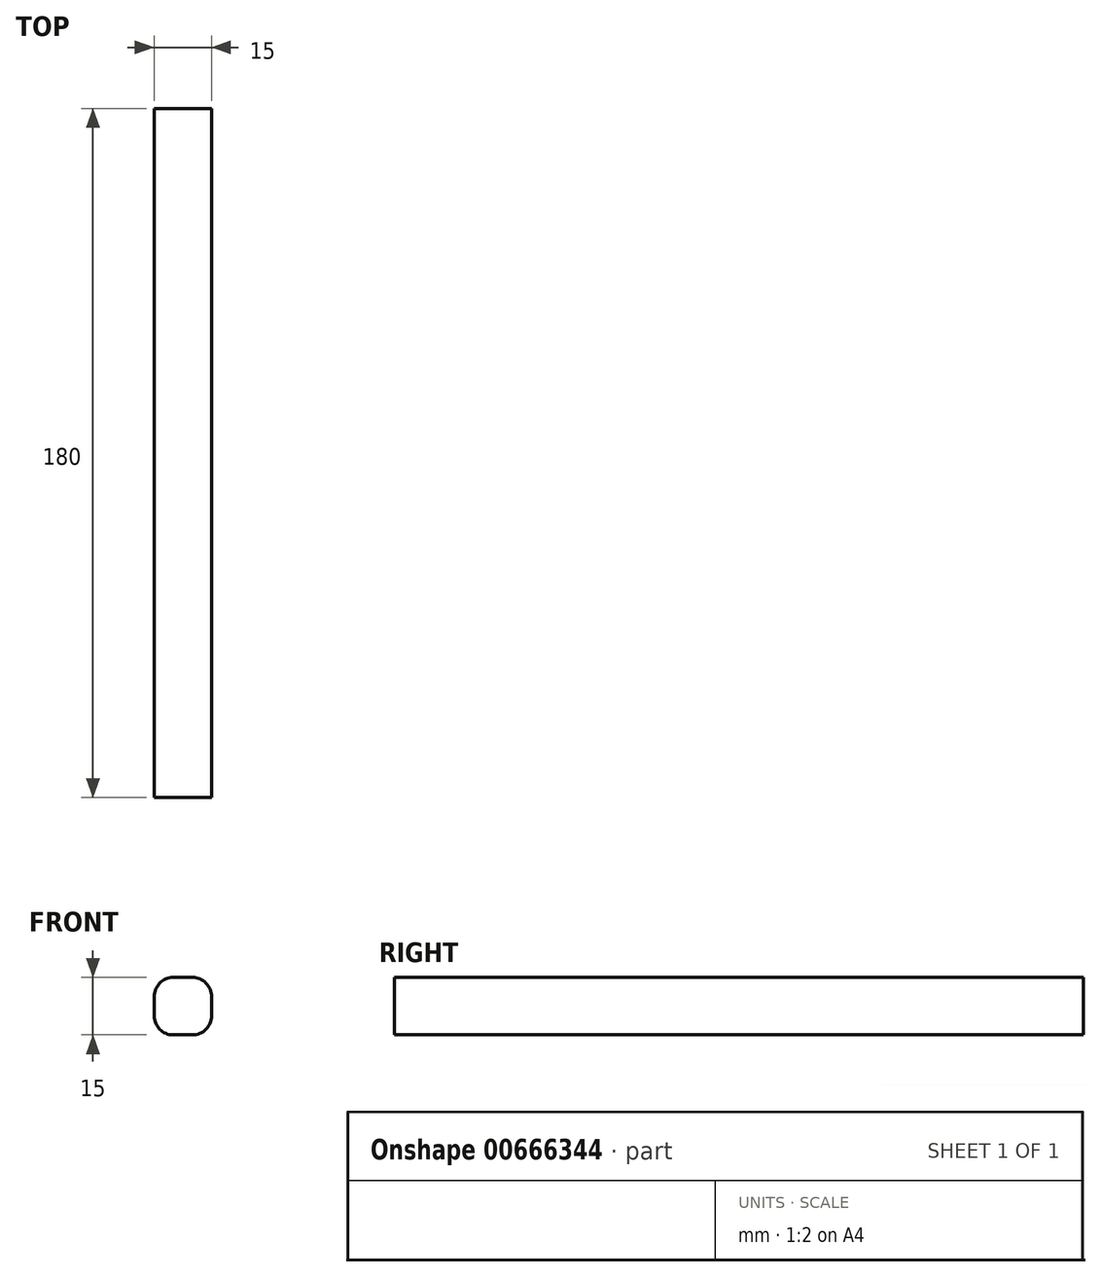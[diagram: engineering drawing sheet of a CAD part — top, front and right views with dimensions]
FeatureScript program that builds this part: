
annotation { "Feature Type Name" : "Feature", "Feature Type Description" : "" }
export const myFeature = defineFeature(function(context is Context, id is Id, definition is map)
    precondition{}
    {
        {
            var Q0;
            Q0=qCreatedBy(makeId("Front.planeOp"),FACE);
            var sketch = newSketch(context, id + "F0", { "sketchPlane" : qUnion([Q0])});
            skLineSegment(sketch, "E0.bottom", {"start": v(2.5, 7.5) * mm, "end": v(-2.5, 7.5) * mm});
            skLineSegment(sketch, "E0.top", {"start": v(2.5, -7.5) * mm, "end": v(-2.5, -7.5) * mm});
            skLineSegment(sketch, "E0.left", {"start": v(7.5, 2.5) * mm, "end": v(7.5, -2.5) * mm});
            skLineSegment(sketch, "E0.right", {"start": v(-7.5, 2.5) * mm, "end": v(-7.5, -2.5) * mm});
            skPoint(sketch, "E0.middle", {"position": v(0, 0) * mm});
            skPoint(sketch, "E1.visualSharp", {"position": v(7.5, 7.5) * mm});
            skArc(sketch, "E1.filletArc", {"start": v(7.5, 2.5) * mm, "mid": v(6.04, 6.04) * mm, "end": v(2.5, 7.5) * mm});
            skPoint(sketch, "E2.visualSharp", {"position": v(7.5, -7.5) * mm});
            skArc(sketch, "E2.filletArc", {"start": v(2.5, -7.5) * mm, "mid": v(6.04, -6.04) * mm, "end": v(7.5, -2.5) * mm});
            skPoint(sketch, "E3.visualSharp", {"position": v(-7.5, -7.5) * mm});
            skArc(sketch, "E3.filletArc", {"start": v(-7.5, -2.5) * mm, "mid": v(-6.04, -6.04) * mm, "end": v(-2.5, -7.5) * mm});
            skPoint(sketch, "E4.visualSharp", {"position": v(-7.5, 7.5) * mm});
            skArc(sketch, "E4.filletArc", {"start": v(-2.5, 7.5) * mm, "mid": v(-6.04, 6.04) * mm, "end": v(-7.5, 2.5) * mm});
            skSolve(sketch);
        }
        {
            var Q0;
            Q0=makeQuery(id+"F0.imprint","IMPRINT",FACE,{"disambiguationData":[TD([[makeQuery(id+"F0.imprint","IMPRINT",EDGE,{"derivedFrom":sQuery(id+"F0.wireOp",EDGE,"E0.bottom")}),1.0]])]});
            extrude(context, id + "F1", {"entities" : qUnion([Q0]), "depth" : 180 * mm, "offsetDistance" : 25 * mm});
        }
    });
